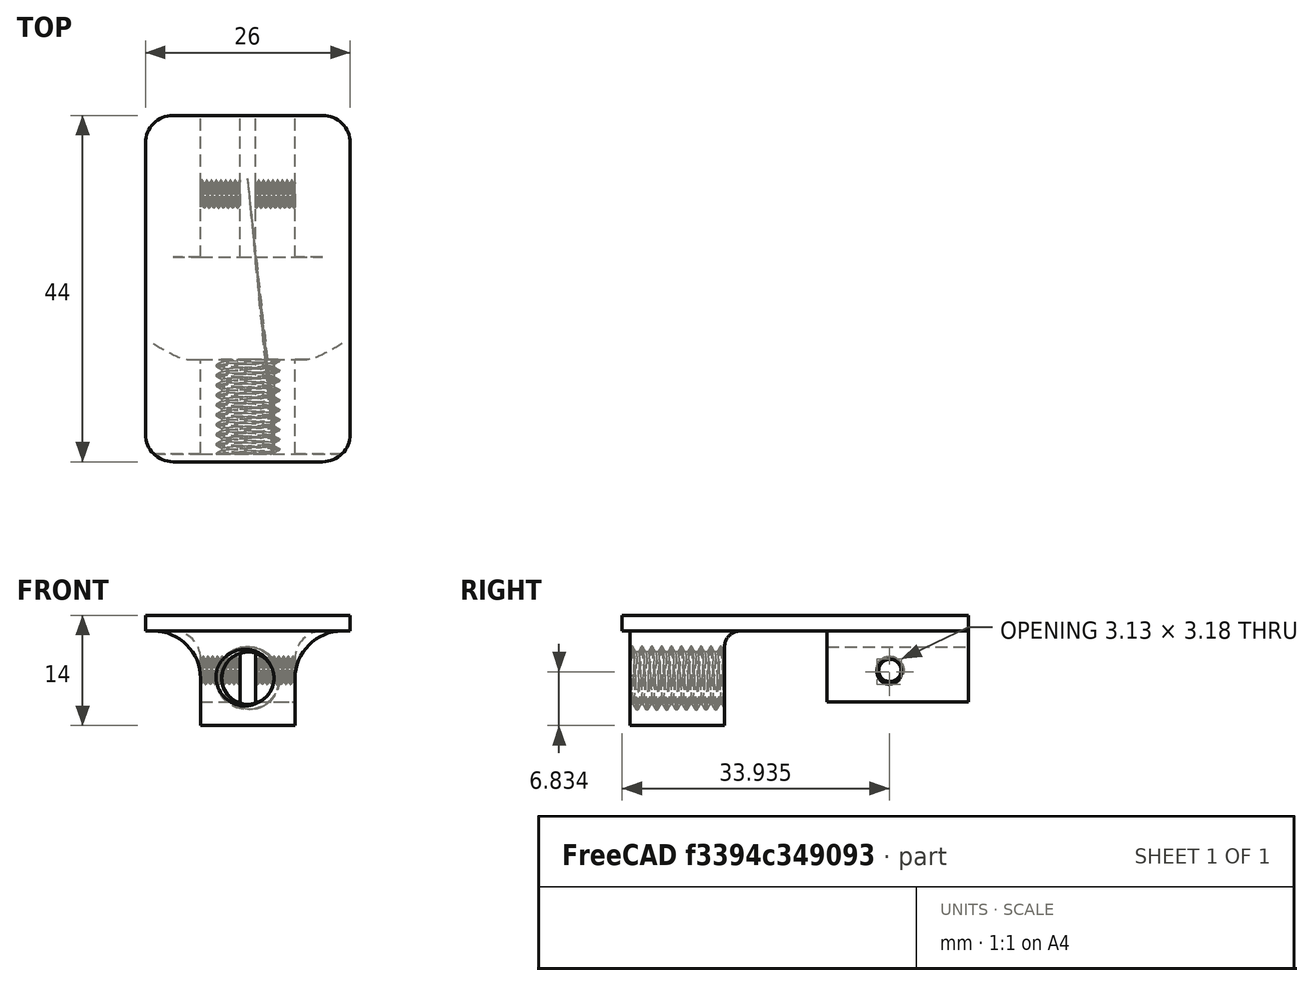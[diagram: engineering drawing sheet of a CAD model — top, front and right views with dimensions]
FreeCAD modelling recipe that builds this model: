
FCSTD DOCUMENT  (FreeCAD 0.18.4R)
Label: Weight
License: All rights reserved
LicenseURL: http://en.wikipedia.org/wiki/All_rights_reserved
objects: Part::Box×4, Part::Fillet×4, Part::Cut×3, Part::FeaturePython×2, Part::MultiFuse×2
note: 15 computed .brp shape members not serialized (recipe doc carries the construction recipe); baked Part::Feature solids carry a one-line shape summary decoded from their .brp

FEATURE [Part::Box] Box062  label="Cube062"
  AttacherType = Attacher::AttachEngine3D
  Height = 12
  Length = 12
  Placement = pos=(-6,-27,-12) rot=(0,0,1;0rad)
  Width = 12
FEATURE [Part::FeaturePython] ScrewTap031  label="M8x20.0-ScrewTap"  # Fasteners workbench fastener (typed FeaturePython)
  Placement = pos=(0,-14,-6) rot=(-1,0,0;1.5708rad)
  diameter = 9
  invert = false
  length = 20
  matchOuter = false
  offset = 0
  thread = true
FEATURE [Part::Cut] Cut080
  Base = -> Box062
  Placement = pos=(0,-8,0) rot=(0,0,1;0rad)
  Tool = -> ScrewTap031
FEATURE [Part::Box] Box063  label="Cube063"
  AttacherType = Attacher::AttachEngine3D
  Height = 2
  Length = 26
  Placement = pos=(-13,-36,0) rot=(0,0,1;0rad)
  Width = 44
FEATURE [Part::MultiFuse] Fusion028
  Shapes = -> [Cut080,Box063]
FEATURE [Part::Fillet] Fillet016
  Base = -> Fusion028
  Edges = 2 edges r=6: [Edge13,Edge15]
FEATURE [Part::Box] Box064  label="Cube064"
  AttacherType = Attacher::AttachEngine3D
  Height = 9
  Length = 12
  Placement = pos=(16,23,-7) rot=(0,0,1;0rad)
  Width = 18
FEATURE [Part::Box] Box065  label="Cube065"
  AttacherType = Attacher::AttachEngine3D
  Height = 7
  Length = 2
  Placement = pos=(21,20.5,-7) rot=(0,0,-1;0rad)
  Width = 25
FEATURE [Part::Cut] Cut081
  Base = -> Box064
  Placement = pos=(-22,-33,-2) rot=(0,0,-1;0rad)
  Tool = -> Box065
FEATURE [Part::MultiFuse] Fusion029
  Shapes = -> [Cut081,Fillet016]
FEATURE [Part::FeaturePython] ScrewTap032  label="(M3.5)x20.0-ScrewTap015"  # Fasteners workbench fastener (typed FeaturePython)
  Placement = pos=(9,-2,-5) rot=(0,1,0;1.5708rad)
  diameter = 5
  invert = false
  length = 20
  matchOuter = false
  offset = 0
  thread = true
FEATURE [Part::Cut] Cut082
  Base = -> Fusion029
  Tool = -> ScrewTap032
FEATURE [Part::Fillet] Fillet017
  Base = -> Cut082
  Edges = 2 edges r=3.5: [Edge2,Edge4]
FEATURE [Part::Fillet] Fillet018
  Base = -> Fillet017
  Edges = 6 edges r=3.5: [Edge19,Edge20,Edge21,Edge24,Edge28,Edge38]
FEATURE [Part::Fillet] Fillet019  label="WeightV1"
  Base = -> Fillet018
  Edges = 2 edges r=2: [Edge20,Edge24]
